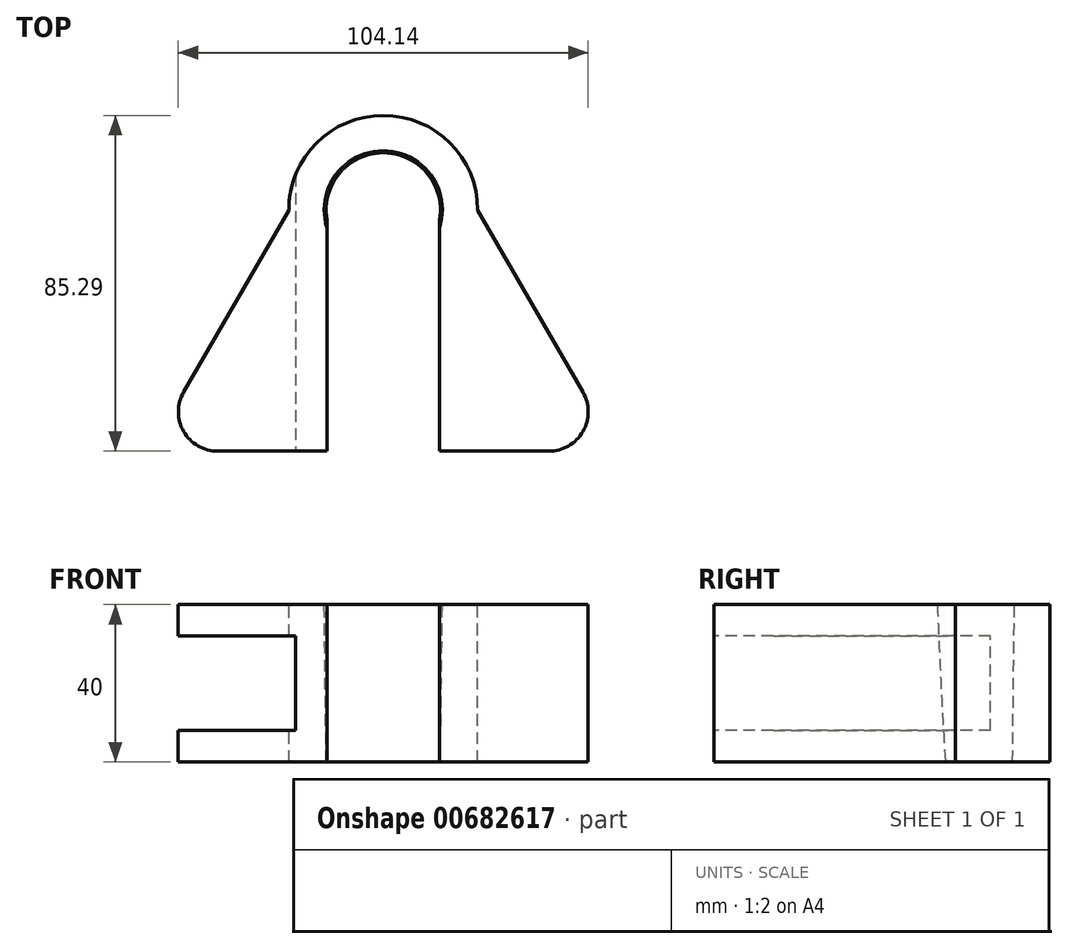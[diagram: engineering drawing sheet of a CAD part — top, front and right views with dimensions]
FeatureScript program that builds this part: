
annotation { "Feature Type Name" : "Feature", "Feature Type Description" : "" }
export const myFeature = defineFeature(function(context is Context, id is Id, definition is map)
    precondition{}
    {
        {
            var Q0;
            Q0=qCreatedBy(makeId("Top.planeOp"),FACE);
            var sketch = newSketch(context, id + "F0", { "sketchPlane" : qUnion([Q0])});
            skCircle(sketch, "E0", {"center": v(0, 0) * mm, "radius": 15 * mm});
            skSolve(sketch);
        }
        {
            var Q0;
            Q0=qCreatedBy(makeId("Top.planeOp"),FACE);
            cPlane(context, id + "F1", {"entities" : qUnion([Q0]), "cplaneType" : CPlaneType.OFFSET, "offset" : 40 * mm, "oppositeDirection" : true, "width" : 150 * mm, "height" : 150 * mm});
        }
        {
            var Q0;
            Q0=qCreatedBy(id+"F1.planeOp",FACE);
            var sketch = newSketch(context, id + "F2", { "sketchPlane" : qUnion([Q0])});
            skCircle(sketch, "E1", {"center": v(0, 0) * mm, "radius": 14.5 * mm});
            skSolve(sketch);
        }
        {
            var Q0;
            Q0=qCreatedBy(makeId("Top.planeOp"),FACE);
            var sketch = newSketch(context, id + "F3", { "sketchPlane" : qUnion([Q0])});
            skCircle(sketch, "E2", {"center": v(0, 0) * mm, "radius": 24 * mm});
            skSolve(sketch);
        }
        {
            var Q0;
            Q0=makeQuery(id+"F3.imprint","IMPRINT",FACE,{"disambiguationData":[TD([[makeQuery(id+"F3.imprint","IMPRINT",EDGE,{"derivedFrom":sQuery(id+"F3.wireOp",EDGE,"E2")}),1.0]])]});
            extrude(context, id + "F4", {"entities" : qUnion([Q0]), "oppositeDirection" : true, "depth" : 40 * mm, "offsetDistance" : 25 * mm});
        }
        {
            var Q0;
            Q0=makeQuery(id+"F0.imprint","IMPRINT",FACE,{"disambiguationData":[TD([[makeQuery(id+"F0.imprint","IMPRINT",EDGE,{"derivedFrom":sQuery(id+"F0.wireOp",EDGE,"E0")}),1.0]])]});
            var Q1;
            Q1=makeQuery(id+"F2.imprint","IMPRINT",FACE,{"disambiguationData":[TD([[makeQuery(id+"F2.imprint","IMPRINT",EDGE,{"derivedFrom":sQuery(id+"F2.wireOp",EDGE,"E1")}),1.0]])]});
            loft(context, id + "F5", {"operationType" : NewBodyOperationType.REMOVE, "sheetProfilesArray" : [{ "sheetProfileEntities" : qUnion([Q0]) }, { "sheetProfileEntities" : qUnion([Q1]) }]});
        }
        {
            var Q0;
            Q0=makeQuery(id+"F4.opExtrude","CAP_FACE",FACE,{"disambiguationData":[OSD([sQuery(id+"F3.wireOp",EDGE,"E2")])],"isStart":true});
            var sketch = newSketch(context, id + "F6", { "sketchPlane" : qUnion([Q0])});
            skCircle(sketch, "E3.0.0", {"center": v(0, 0) * mm, "radius": 24 * mm});
            skCircle(sketch, "E4.0", {"center": v(0, 0) * mm, "radius": 14.5 * mm});
            skCircle(sketch, "E5.0", {"center": v(0, 0) * mm, "radius": 15 * mm});
            skLineSegment(sketch, "E6", {"start": v(0, 0) * mm, "end": v(-14.28, -2.52) * mm});
            skLineSegment(sketch, "E7", {"start": v(0, 0) * mm, "end": v(14.28, -2.52) * mm});
            skLineSegment(sketch, "E8", {"start": v(0, 0) * mm, "end": v(14.5, 0) * mm});
            skLineSegment(sketch, "E9", {"start": v(0, 0) * mm, "end": v(-14.5, 0) * mm});
            skLineSegment(sketch, "E10", {"start": v(-14.28, -2.52) * mm, "end": v(-14.28, -19.29) * mm});
            skLineSegment(sketch, "E11", {"start": v(14.28, -2.52) * mm, "end": v(14.28, -19.29) * mm});
            skSolve(sketch);
        }
        {
            var Q0;
            {var subQ0=sQuery(id+"F6.wireOp",EDGE,"E10");var subQ1=sQuery(id+"F6.wireOp",EDGE,"E5.0");var subQ2=makeQuery(id+"F6.imprint","INTERSECT",VERTEX,{"derivedFrom":[subQ1,subQ0]});Q0=makeQuery(id+"F6.imprint","IMPRINT",FACE,{"disambiguationData":[TD([[makeQuery(id+"F6.imprint","IMPRINT",EDGE,{"disambiguationData":[TD([[subQ2,1.0]])],"derivedFrom":subQ1}),1.0]])]});}
            var Q1;
            {var subQ0=sQuery(id+"F6.wireOp",EDGE,"E10");var subQ5=sQuery(id+"F6.wireOp",EDGE,"E5.0");var subQ6=makeQuery(id+"F6.imprint","INTERSECT",VERTEX,{"derivedFrom":[subQ5,subQ0]});Q1=makeQuery(id+"F6.imprint","IMPRINT",FACE,{"disambiguationData":[TD([[makeQuery(id+"F6.imprint","IMPRINT",EDGE,{"disambiguationData":[TD([[subQ6,1.0]])],"derivedFrom":subQ5}),-1.0]])]});}
            extrude(context, id + "F7", {"entities" : qUnion([Q0, Q1]), "operationType" : NewBodyOperationType.REMOVE, "endBound" : BoundingType.THROUGH_ALL, "oppositeDirection" : true, "depth" : 25 * mm, "offsetDistance" : 25 * mm});
        }
        {
            var Q0;
            Q0=makeQuery(id+"F4.opExtrude","CAP_FACE",FACE,{"disambiguationData":[OSD([sQuery(id+"F3.wireOp",EDGE,"E2")])],"isStart":true});
            var sketch = newSketch(context, id + "F8", { "sketchPlane" : qUnion([Q0])});
            skArc(sketch, "E12.0.0", {"start": v(-14.28, -4.6) * mm, "mid": v(0, 15) * mm, "end": v(14.28, -4.6) * mm});
            skLineSegment(sketch, "E12.0.1", {"start": v(14.28, -4.6) * mm, "end": v(14.28, -19.29) * mm});
            skArc(sketch, "E12.0.2", {"start": v(14.28, -19.29) * mm, "mid": v(0, 24) * mm, "end": v(-14.28, -19.29) * mm});
            skLineSegment(sketch, "E12.0.3", {"start": v(-14.28, -19.29) * mm, "end": v(-14.28, -4.6) * mm});
            skLineSegment(sketch, "E13", {"start": v(-24, 0) * mm, "end": v(-59.39, -61.29) * mm});
            skLineSegment(sketch, "E14", {"start": v(-59.39, -61.29) * mm, "end": v(-14.28, -61.29) * mm});
            skLineSegment(sketch, "E15", {"start": v(59.39, -61.29) * mm, "end": v(24, 0) * mm});
            skLineSegment(sketch, "E16", {"start": v(-14.28, -19.29) * mm, "end": v(-14.28, -61.29) * mm});
            skLineSegment(sketch, "E17", {"start": v(14.28, -19.29) * mm, "end": v(14.28, -61.29) * mm});
            skLineSegment(sketch, "E18.trimOffspring", {"start": v(14.28, -61.29) * mm, "end": v(59.39, -61.29) * mm});
            skSolve(sketch);
        }
        {
            var Q0;
            {var subQ2=sQuery(id+"F8.wireOp",EDGE,"E13");Q0=makeQuery(id+"F8.imprint","IMPRINT",FACE,{"disambiguationData":[TD([[makeQuery(id+"F8.imprint","IMPRINT",EDGE,{"derivedFrom":subQ2}),1.0]])]});}
            var Q1;
            {var subQ2=sQuery(id+"F8.wireOp",EDGE,"E15");Q1=makeQuery(id+"F8.imprint","IMPRINT",FACE,{"disambiguationData":[TD([[makeQuery(id+"F8.imprint","IMPRINT",EDGE,{"derivedFrom":subQ2}),1.0]])]});}
            extrude(context, id + "F9", {"entities" : qUnion([Q0, Q1]), "operationType" : NewBodyOperationType.ADD, "oppositeDirection" : true, "depth" : 40 * mm, "offsetDistance" : 25 * mm});
        }
        {
            var Q0;
            Q0=makeQuery(id+"F9.opExtrude","SWEPT_FACE",FACE,{"disambiguationData":[OSD([sQuery(id+"F8.wireOp",EDGE,"E14")])]});
            var sketch = newSketch(context, id + "F10", { "sketchPlane" : qUnion([Q0])});
            skLineSegment(sketch, "E19.bottom", {"start": v(-22.28, -8) * mm, "end": v(-62.28, -8) * mm});
            skLineSegment(sketch, "E19.top", {"start": v(-22.28, -32) * mm, "end": v(-62.28, -32) * mm});
            skLineSegment(sketch, "E19.left", {"start": v(-22.28, -8) * mm, "end": v(-22.28, -32) * mm});
            skLineSegment(sketch, "E19.right", {"start": v(-62.28, -8) * mm, "end": v(-62.28, -32) * mm});
            skLineSegment(sketch, "E20.0.0", {"start": v(-14.28, 0) * mm, "end": v(-59.39, 0) * mm});
            skLineSegment(sketch, "E20.0.1", {"start": v(-59.39, 0) * mm, "end": v(-59.39, -40) * mm});
            skLineSegment(sketch, "E20.0.2", {"start": v(-59.39, -40) * mm, "end": v(-14.28, -40) * mm});
            skLineSegment(sketch, "E20.0.3", {"start": v(-14.28, -40) * mm, "end": v(-14.28, 0) * mm});
            skSolve(sketch);
        }
        {
            var Q0;
            {var subQ0=sQuery(id+"F10.wireOp",EDGE,"E19.left");Q0=makeQuery(id+"F10.imprint","IMPRINT",FACE,{"disambiguationData":[TD([[makeQuery(id+"F10.imprint","IMPRINT",EDGE,{"derivedFrom":subQ0}),-1.0]])]});}
            extrude(context, id + "F11", {"entities" : qUnion([Q0]), "operationType" : NewBodyOperationType.REMOVE, "endBound" : BoundingType.THROUGH_ALL, "oppositeDirection" : true, "depth" : 25 * mm, "offsetDistance" : 25 * mm});
        }
        {
            var Q0;
            {var subQ1=sQuery(id+"F8.wireOp",EDGE,"E13");var subQ2=sQuery(id+"F8.wireOp",EDGE,"E14");Q0=makeQuery(id+"F11.boolean.opBoolean","SPLIT",EDGE,{"disambiguationData":[TD([makeQuery(id+"F4.opExtrude","CAP_FACE",FACE,{"disambiguationData":[OSD([sQuery(id+"F3.wireOp",EDGE,"E2")])],"isStart":true})])],"derivedFrom":makeQuery(id+"F9.opExtrude","SWEPT_EDGE",EDGE,{"disambiguationData":[OSD([subQ1,subQ2])]})});}
            var Q1;
            {var subQ0=sQuery(id+"F8.wireOp",EDGE,"E13");var subQ2=sQuery(id+"F8.wireOp",EDGE,"E14");Q1=makeQuery(id+"F11.boolean.opBoolean","SPLIT",EDGE,{"disambiguationData":[TD([makeQuery(id+"F4.opExtrude","CAP_FACE",FACE,{"disambiguationData":[OSD([sQuery(id+"F3.wireOp",EDGE,"E2")])],"isStart":false})])],"derivedFrom":makeQuery(id+"F9.opExtrude","SWEPT_EDGE",EDGE,{"disambiguationData":[OSD([subQ0,subQ2])]})});}
            var Q2;
            {var subQ0=sQuery(id+"F8.wireOp",EDGE,"E12.0.2");var subQ1=sQuery(id+"F3.wireOp",EDGE,"E2");var subQ2=sQuery(id+"F8.wireOp",EDGE,"E13");Q2=makeQuery(id+"F11.boolean.opBoolean","SPLIT",EDGE,{"disambiguationData":[TD([makeQuery(id+"F4.opExtrude","CAP_FACE",FACE,{"disambiguationData":[OSD([subQ1])],"isStart":true})])],"derivedFrom":makeQuery(id+"F9.opExtrude","SWEPT_EDGE",EDGE,{"disambiguationData":[OSD([subQ0,subQ2])]})});}
            var Q3;
            {var subQ0=sQuery(id+"F8.wireOp",EDGE,"E12.0.2");var subQ1=sQuery(id+"F8.wireOp",EDGE,"E13");var subQ2=sQuery(id+"F3.wireOp",EDGE,"E2");Q3=makeQuery(id+"F11.boolean.opBoolean","SPLIT",EDGE,{"disambiguationData":[TD([makeQuery(id+"F4.opExtrude","CAP_FACE",FACE,{"disambiguationData":[OSD([subQ2])],"isStart":false})])],"derivedFrom":makeQuery(id+"F9.opExtrude","SWEPT_EDGE",EDGE,{"disambiguationData":[OSD([subQ0,subQ1])]})});}
            fillet(context, id + "F12", {"entities" : qUnion([Q0, Q1, Q2, Q3]), "radius" : 10 * mm, "tangentPropagation" : true, "allowEdgeOverflow" : false});
        }
        {
            var Q0;
            {var subQ0=sQuery(id+"F8.wireOp",EDGE,"E15");var subQ1=sQuery(id+"F8.wireOp",EDGE,"E18.trimOffspring");Q0=makeQuery(id+"F1zPADby32qs8xG_1.1.F11.boolean.opBoolean","SPLIT",EDGE,{"disambiguationData":[TD([makeQuery(id+"F4.opExtrude","CAP_FACE",FACE,{"disambiguationData":[OSD([sQuery(id+"F3.wireOp",EDGE,"E2")])],"isStart":true})])],"derivedFrom":makeQuery(id+"F9.opExtrude","SWEPT_EDGE",EDGE,{"disambiguationData":[OSD([subQ0,subQ1])]})});}
            var Q1;
            {var subQ0=sQuery(id+"F8.wireOp",EDGE,"E18.trimOffspring");var subQ1=sQuery(id+"F8.wireOp",EDGE,"E15");Q1=makeQuery(id+"F1zPADby32qs8xG_1.1.F11.boolean.opBoolean","SPLIT",EDGE,{"disambiguationData":[TD([makeQuery(id+"F4.opExtrude","CAP_FACE",FACE,{"disambiguationData":[OSD([sQuery(id+"F3.wireOp",EDGE,"E2")])],"isStart":false})])],"derivedFrom":makeQuery(id+"F9.opExtrude","SWEPT_EDGE",EDGE,{"disambiguationData":[OSD([subQ1,subQ0])]})});}
            var Q2;
            {var subQ0=sQuery(id+"F8.wireOp",EDGE,"E15");var subQ1=sQuery(id+"F8.wireOp",EDGE,"E12.0.2");var subQ2=sQuery(id+"F3.wireOp",EDGE,"E2");Q2=makeQuery(id+"F1zPADby32qs8xG_1.1.F11.boolean.opBoolean","SPLIT",EDGE,{"disambiguationData":[TD([makeQuery(id+"F4.opExtrude","CAP_FACE",FACE,{"disambiguationData":[OSD([subQ2])],"isStart":true})])],"derivedFrom":makeQuery(id+"F9.opExtrude","SWEPT_EDGE",EDGE,{"disambiguationData":[OSD([subQ1,subQ0])]})});}
            var Q3;
            {var subQ0=sQuery(id+"F8.wireOp",EDGE,"E15");var subQ1=sQuery(id+"F8.wireOp",EDGE,"E12.0.2");var subQ2=sQuery(id+"F3.wireOp",EDGE,"E2");Q3=makeQuery(id+"F1zPADby32qs8xG_1.1.F11.boolean.opBoolean","SPLIT",EDGE,{"disambiguationData":[TD([makeQuery(id+"F4.opExtrude","CAP_FACE",FACE,{"disambiguationData":[OSD([subQ2])],"isStart":false})])],"derivedFrom":makeQuery(id+"F9.opExtrude","SWEPT_EDGE",EDGE,{"disambiguationData":[OSD([subQ1,subQ0])]})});}
            fillet(context, id + "F13", {"entities" : qUnion([Q0, Q1, Q2, Q3]), "radius" : 10 * mm, "tangentPropagation" : true, "allowEdgeOverflow" : false});
        }
    });
